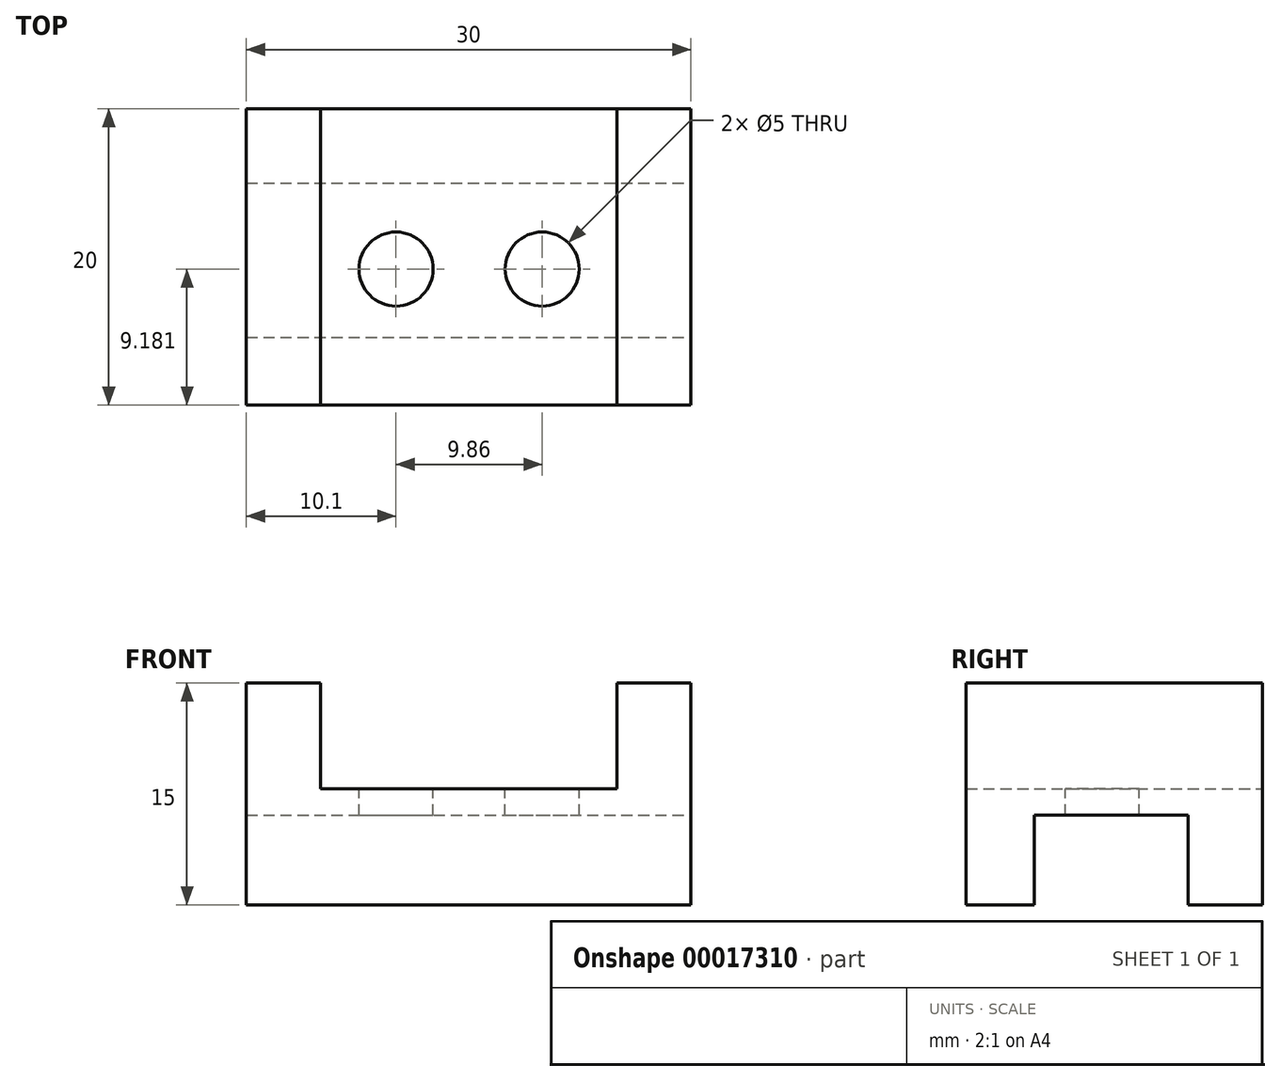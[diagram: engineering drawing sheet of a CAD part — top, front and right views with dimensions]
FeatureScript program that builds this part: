
annotation { "Feature Type Name" : "Feature", "Feature Type Description" : "" }
export const myFeature = defineFeature(function(context is Context, id is Id, definition is map)
    precondition{}
    {
        {
            var Q0;
            Q0=qCreatedBy(makeId("Front.planeOp"),FACE);
            var sketch = newSketch(context, id + "F0", { "sketchPlane" : qUnion([Q0])});
            skLineSegment(sketch, "E0", {"start": v(-22.2, 7.15) * mm, "end": v(-22.2, -7.85) * mm});
            skLineSegment(sketch, "E1", {"start": v(7.8, -7.85) * mm, "end": v(7.8, 7.15) * mm});
            skLineSegment(sketch, "E2", {"start": v(-22.2, 7.15) * mm, "end": v(-17.2, 7.15) * mm});
            skLineSegment(sketch, "E3", {"start": v(-17.2, 7.15) * mm, "end": v(-17.2, 0) * mm});
            skLineSegment(sketch, "E4", {"start": v(-17.2, 0) * mm, "end": v(2.8, 0) * mm});
            skLineSegment(sketch, "E5", {"start": v(2.8, 0) * mm, "end": v(2.8, 7.15) * mm});
            skLineSegment(sketch, "E6", {"start": v(2.8, 7.15) * mm, "end": v(7.8, 7.15) * mm});
            skLineSegment(sketch, "E7", {"start": v(-22.2, -7.85) * mm, "end": v(7.8, -7.85) * mm});
            skSolve(sketch);
        }
        {
            var Q0;
            Q0 = qSketchRegion(id + "F0", true);
            extrude(context, id + "F1", {"entities" : qUnion([Q0]), "depth" : 20 * mm});
        }
        {
            var Q0;
            Q0=makeQuery(id+"F1.opExtrude","SWEPT_FACE",FACE,{"disambiguationData":[OSD([sQuery(id+"F0.wireOp",EDGE,"E1")])]});
            var sketch = newSketch(context, id + "F2", { "sketchPlane" : qUnion([Q0])});
            skLineSegment(sketch, "E8.top", {"start": v(-15.42, -1.8) * mm, "end": v(-5.02, -1.8) * mm});
            skLineSegment(sketch, "E8.left", {"start": v(-15.42, -7.85) * mm, "end": v(-15.42, -1.8) * mm});
            skLineSegment(sketch, "E8.right", {"start": v(-5.02, -7.85) * mm, "end": v(-5.02, -1.8) * mm});
            skSolve(sketch);
        }
        {
            var Q0;
            Q0=makeQuery(id+"F2.imprint","IMPRINT",FACE,{"disambiguationData":[TD([[makeQuery(id+"F2.imprint","IMPRINT",EDGE,{"derivedFrom":sQuery(id+"F2.wireOp",EDGE,"E8.top")}),-1.0]])]});
            extrude(context, id + "F3", {"entities" : qUnion([Q0]), "operationType" : NewBodyOperationType.REMOVE, "endBound" : BoundingType.THROUGH_ALL, "oppositeDirection" : true, "depth" : 25 * mm});
        }
        {
            var Q0;
            Q0=makeQuery(id+"F1.opExtrude","SWEPT_FACE",FACE,{"disambiguationData":[OSD([sQuery(id+"F0.wireOp",EDGE,"E4")])]});
            var sketch = newSketch(context, id + "F4", { "sketchPlane" : qUnion([Q0])});
            skCircle(sketch, "E9", {"center": v(-12.1, -10.82) * mm, "radius": 2.5 * mm});
            skCircle(sketch, "E10", {"center": v(-2.24, -10.82) * mm, "radius": 2.5 * mm});
            skSolve(sketch);
        }
        {
            var Q0;
            Q0=makeQuery(id+"F4.imprint","IMPRINT",FACE,{"disambiguationData":[TD([[makeQuery(id+"F4.imprint","IMPRINT",EDGE,{"derivedFrom":sQuery(id+"F4.wireOp",EDGE,"E9")}),1.0]])]});
            var Q1;
            Q1=makeQuery(id+"F4.imprint","IMPRINT",FACE,{"disambiguationData":[TD([[makeQuery(id+"F4.imprint","IMPRINT",EDGE,{"derivedFrom":sQuery(id+"F4.wireOp",EDGE,"E10")}),1.0]])]});
            extrude(context, id + "F5", {"entities" : qUnion([Q0, Q1]), "operationType" : NewBodyOperationType.REMOVE, "endBound" : BoundingType.THROUGH_ALL, "oppositeDirection" : true, "depth" : 25 * mm});
        }
    });
